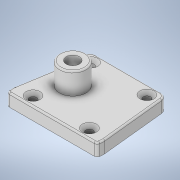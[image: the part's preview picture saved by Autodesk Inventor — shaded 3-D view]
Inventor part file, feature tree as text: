
AUTODESK INVENTOR PART (.ipt)
format: ipt  version: 2020.3 (Build 243373000, 373)  size: 357,376 bytes
history: native  units: mm
features: sketch x3, extrude x3, hole x3, fillet x2
ambient origin geometry x8: Origin, YZ Plane, XZ Plane, XY Plane, X Axis, Y Axis, Z Axis, Center Point
bodies: Body1 (feature_tree)
feature tree (11):
  sketch  "Sketch1"  dims[d0=135.0deg d4=24.6mm]
  extrude  "Extrusion12"  Depth=24.6mm
  extrude  "Extrusion13"  Depth=70.0mm
  extrude  "Extrusion14"  Depth=6.5mm
  hole  "Hole3"  [1 undecoded]
  fillet  "Fillet10"  Radius=6.0mm
  fillet  "Fillet11"  Radius=2.0mm
  hole  "Hole4"  [1 undecoded]
  hole  "Hole5"  [1 undecoded]
  sketch  "Sketch2"  dims[d5=12.4mm d6=70.0mm]
  sketch  "Sketch4"  dims[d7=60.0mm d9=8.5mm d10=135.0deg d12=6.0mm d13=2.0mm d14=2.0mm d16=20.0mm d23=5.0mm d29=130.0mm d32=15.0mm d33=4.0mm d34=28.4mm d38=4.0mm d40=6.8mm d49=30.0mm d50=84.0mm d51=3.0mm d52=3.0mm d53=1.5mm d54=20.0mm d59=1.0mm d60=90.0mm d61=135.0deg d70=135.0deg d82=0.7mm d83=0.7mm d84=0.7mm d85=0.7mm d86=6.0mm d102=18.0mm d103=4.0mm d104=0.0mm d105=4.0mm d106=0.0mm d107=10.9mm d108=0.0mm d116=4.2mm d117=6.0mm d118=5.6mm d119=0.85mm d120=90.0deg d121=4.2mm d122=0.0mm d123=2.0mm d125=0.5mm d126=2.0mm d128=1.0mm d135=2.3mm d136=6.0mm d137=4.5mm d138=2.0mm d139=90.0deg d140=6.5mm d141=0.0mm d142=5.6mm d143=6.0mm d144=9.0mm d145=1.0mm d146=90.0deg d147=6.5mm d148=0.0mm]
note: 3 required parameter values undecoded (feature->parameter linkage not recoverable at this tier; creation-order binding heuristic only, values carry confidence <= 0.55)
